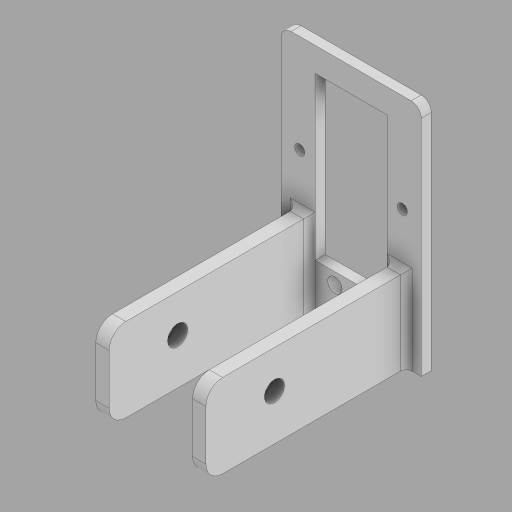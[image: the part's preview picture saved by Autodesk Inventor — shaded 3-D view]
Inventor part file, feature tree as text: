
AUTODESK INVENTOR PART (.ipt)
format: ipt  version: 2023.2 (Build 272271030, 271C)  size: 681,984 bytes
history: native  units: mm
features: sketch x19, extrude x18, projected_geometry x16, fillet x3
ambient origin geometry x8: Origin, YZ Plane, XZ Plane, XY Plane, X Axis, Y Axis, Z Axis, Center Point
bodies: Solid1 (feature_tree)
feature tree (56):
  sketch  "Sketch1"  dims[d0=42.0mm d1=70.0mm d4=21.5mm]
  extrude  "Extrusion1"  Depth=70.0mm
  fillet  "Fillet3"  Radius=21.5mm
  extrude  "Extrusion11"  Depth=2.0mm TaperAngle=0.0deg
  extrude  "Extrusion12"  Depth=3.0mm
  extrude  "Extrusion15"  Depth=4.3mm
  extrude  "Extrusion16"  Depth=9.7mm
  sketch  "Sketch22"  dims[d55=4.3mm d56=9.7mm]
  extrude  "Extrusion20"  Depth=7.0mm
  extrude  "Extrusion22"  Depth=4.625mm
  extrude  "Extrusion23"  Depth=3.0mm
  extrude  "Extrusion24"  Depth=10.0mm
  sketch  "Sketch30"  dims[d88=7.0mm d89=10.0mm d90=0.0mm]
  extrude  "Extrusion27"  Depth=10.0mm TaperAngle=0.0deg
  sketch  "Sketch36"  dims[d103=20.0mm d104=42.0mm d105=0.0mm d106=26.0mm]
  sketch  "Sketch37"  dims[d107=42.0mm d108=0.0mm d112=19.0mm]
  extrude  "Extrusion29"  Depth=60.0mm TaperAngle=0.0deg
  extrude  "Extrusion31"  Depth=42.0mm TaperAngle=0.0deg
  fillet  "Fillet15"  Radius=26.0mm
  extrude  "Extrusion32"  Depth=42.0mm
  extrude  "Extrusion33"  Depth=25.0mm
  extrude  "Extrusion34"  Depth=60.0mm TaperAngle=0.0deg
  extrude  "Extrusion35"  Depth=5.0mm
  extrude  "Extrusion36"  Depth=60.0mm TaperAngle=0.0deg
  fillet  "Fillet18"  Radius=0.5mm
  extrude  "Extrusion38"  Depth=0.5mm TaperAngle=0.0deg
  sketch  "Sketch14"  dims[d5=41.5mm d6=2.0mm d7=0.0mm]
  projected_geometry  "Projected Loop9"
  sketch  "Sketch17"  dims[d18=3.85mm d38=3.0mm]
  projected_geometry  "Projected Loop12"
  sketch  "Sketch18"  dims[d52=6.0mm d53=0.0mm d54=4.3mm]
  projected_geometry  "Projected Loop13"
  sketch  "Sketch23"  dims[d59=6.0mm d60=0.0mm d67=7.0mm]
  projected_geometry  "Projected Loop15"
  sketch  "Sketch25"  dims[d68=6.0mm d69=0.0mm d70=4.625mm]
  sketch  "Sketch26"  dims[d71=28.375mm d72=3.0mm]
  projected_geometry  "Projected Loop17"
  sketch  "Sketch27"  dims[d73=10.0mm d74=0.0mm d75=30.75mm]
  projected_geometry  "Projected Loop18"
  sketch  "Sketch34"  dims[d97=42.0mm d98=60.0mm d99=2.0mm d100=0.0mm d101=0.0mm]
  projected_geometry  "Projected Loop21"
  projected_geometry  "Projected Loop23"
  sketch  "Sketch39"  dims[d119=7.0mm d120=25.0mm]
  projected_geometry  "Projected Loop25"
  projected_geometry  "Projected Loop27"
  sketch  "Sketch40"  dims[d122=1.0mm d123=0.0mm d127=60.0mm d128=0.0mm]
  projected_geometry  "Projected Loop28"
  projected_geometry  "Projected Loop29"
  sketch  "Sketch41"  dims[d131=42.0mm d132=0.0mm d133=5.0mm]
  projected_geometry  "Projected Loop30"
  sketch  "Sketch42"  dims[d135=60.0mm d136=0.0mm d138=0.5mm d139=0.0mm d140=0.5mm d141=0.0mm]
  projected_geometry  "Projected Loop31"
  sketch  "Sketch43"  dims[d143=0.5mm d144=0.0mm d145=0.5mm d146=0.0mm]
  projected_geometry  "Projected Loop32"
  sketch  "Sketch45"  dims[d147=1.75mm d153=17.298mm d154=11.289mm d155=6.0mm d156=100.0mm d157=0.0mm d158=20.5mm d39=0.5mm d40=0.872665mm d41=0.5mm d42=0.872665mm d113=0.872665mm d114=0.5mm d115=0.872665mm]
  projected_geometry  "Projected Loop34"
